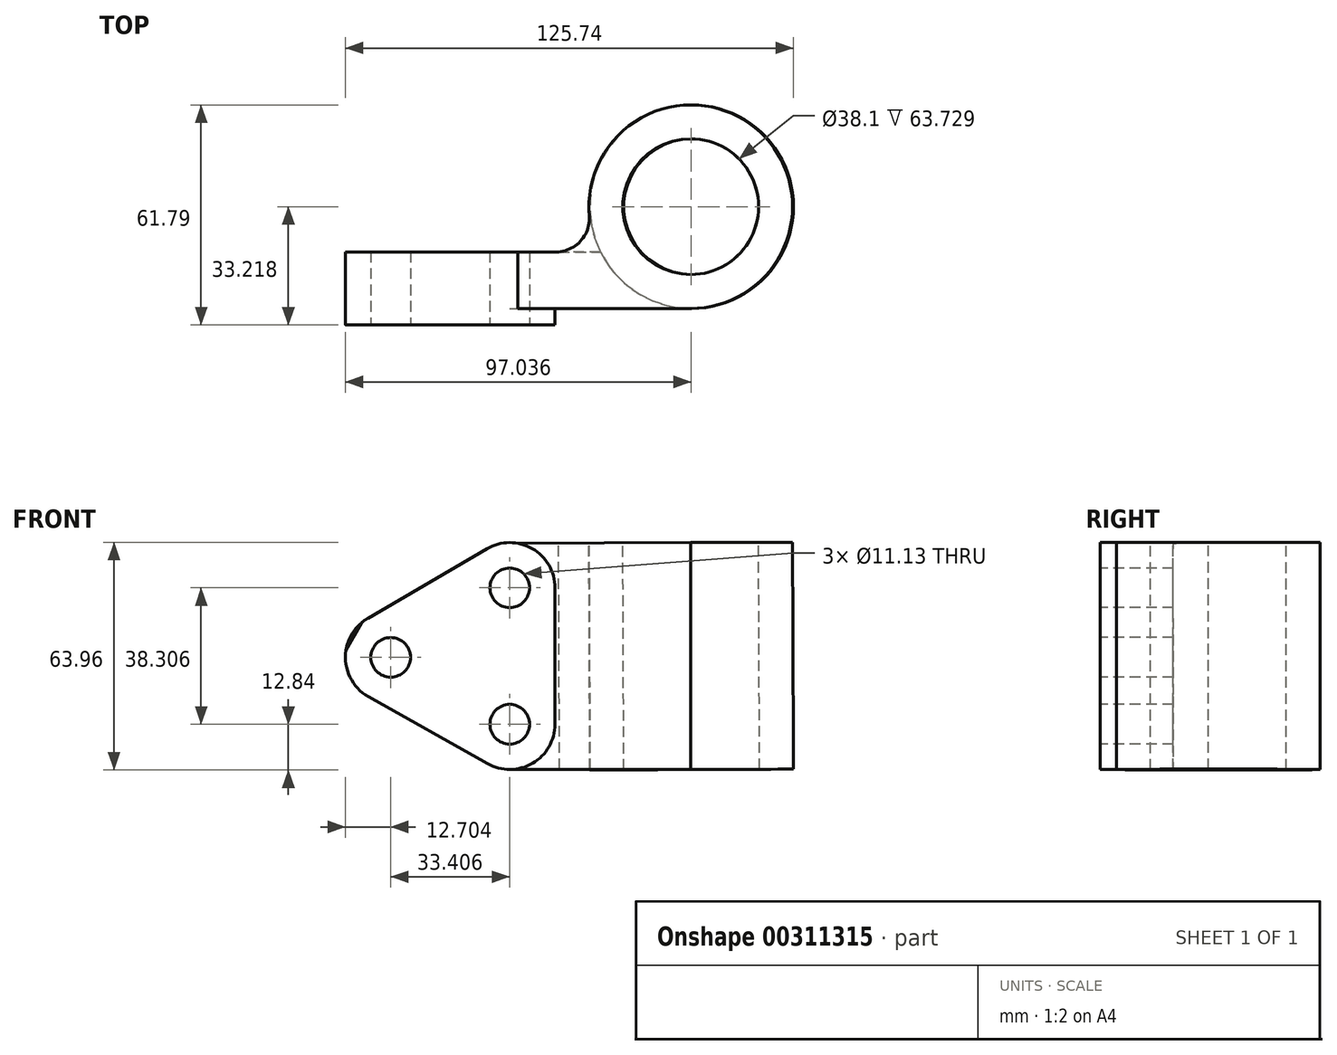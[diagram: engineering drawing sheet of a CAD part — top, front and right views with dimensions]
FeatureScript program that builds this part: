
annotation { "Feature Type Name" : "Feature", "Feature Type Description" : "" }
export const myFeature = defineFeature(function(context is Context, id is Id, definition is map)
    precondition{}
    {
        {
            var Q0;
            Q0=qCreatedBy(makeId("Front.planeOp"),FACE);
            var sketch = newSketch(context, id + "F0", { "sketchPlane" : qUnion([Q0])});
            skLineSegment(sketch, "E0", {"start": v(0, 0) * mm, "end": v(0, 63.5) * mm});
            skLineSegment(sketch, "E1", {"start": v(0, 0) * mm, "end": v(50.8, 0) * mm});
            skLineSegment(sketch, "E2", {"start": v(50.8, 0) * mm, "end": v(50.8, 63.7) * mm});
            skLineSegment(sketch, "E3", {"start": v(50.8, 63.7) * mm, "end": v(0, 63.5) * mm});
            skSolve(sketch);
        }
        {
            var Q0;
            Q0 = qSketchRegion(id + "F0", true);
            extrude(context, id + "F1", {"entities" : qUnion([Q0]), "endBound" : BoundingType.SYMMETRIC, "depth" : 15.88 * mm});
        }
        {
            var Q0;
            Q0=makeQuery(id+"F1.opExtrude","CAP_FACE",FACE,{"disambiguationData":[OSD([sQuery(id+"F0.wireOp",EDGE,"E0"),sQuery(id+"F0.wireOp",EDGE,"E1"),sQuery(id+"F0.wireOp",EDGE,"E2"),sQuery(id+"F0.wireOp",EDGE,"E3")])],"isStart":false});
            var sketch = newSketch(context, id + "F2", { "sketchPlane" : qUnion([Q0])});
            skCircle(sketch, "E4", {"center": v(-33.4, 31.49) * mm, "radius": 12.7 * mm});
            skCircle(sketch, "E5", {"center": v(0, 12.7) * mm, "radius": 12.7 * mm});
            skCircle(sketch, "E6", {"center": v(0, 51) * mm, "radius": 12.7 * mm});
            skLineSegment(sketch, "E7", {"start": v(-39.63, 20.42) * mm, "end": v(-6.23, 1.63) * mm});
            skLineSegment(sketch, "E8", {"start": v(-39.81, 42.46) * mm, "end": v(-6.4, 61.97) * mm});
            skLineSegment(sketch, "E9", {"start": v(12.7, 51) * mm, "end": v(12.7, 12.7) * mm});
            skSolve(sketch);
        }
        {
            var Q0;
            Q0 = qSketchRegion(id + "F2", true);
            extrude(context, id + "F3", {"entities" : qUnion([Q0]), "operationType" : NewBodyOperationType.ADD, "endBound" : BoundingType.SYMMETRIC, "oppositeDirection" : true, "depth" : 31.75 * mm});
        }
        {
            var Q0;
            Q0=makeQuery(id+"F3.opExtrude","SWEPT_FACE",FACE,{"disambiguationData":[OSD([sQuery(id+"F2.wireOp",EDGE,"E7")])]});
            var sketch = newSketch(context, id + "F4", { "sketchPlane" : qUnion([Q0])});
            skLineSegment(sketch, "E10", {"start": v(15.5, 7.79) * mm, "end": v(15.5, 12.56) * mm, "construction": true});
            skLineSegment(sketch, "E11", {"start": v(15.5, 12.56) * mm, "end": v(-56.45, 12.56) * mm});
            skLineSegment(sketch, "E12", {"start": v(-56.45, 12.56) * mm, "end": v(-56.45, 26.24) * mm});
            skLineSegment(sketch, "E13", {"start": v(-56.45, 26.24) * mm, "end": v(15.5, 26.24) * mm});
            skLineSegment(sketch, "E14", {"start": v(15.5, 26.24) * mm, "end": v(15.5, 12.56) * mm});
            skSolve(sketch);
        }
        {
            var Q0;
            Q0 = qSketchRegion(id + "F4", true);
            extrude(context, id + "F5", {"entities" : qUnion([Q0]), "operationType" : NewBodyOperationType.REMOVE, "oppositeDirection" : true, "depth" : 87.88 * mm});
        }
        {
            var Q0;
            Q0=qCreatedBy(makeId("Top.planeOp"),FACE);
            var sketch = newSketch(context, id + "F6", { "sketchPlane" : qUnion([Q0])});
            skLineSegment(sketch, "E15", {"start": v(-41.44, -12.58) * mm, "end": v(-46.1, -12.58) * mm});
            skLineSegment(sketch, "E16", {"start": v(-46.1, -12.58) * mm, "end": v(-46.1, -26.86) * mm});
            skLineSegment(sketch, "E17", {"start": v(-46.1, -26.86) * mm, "end": v(-39.63, -26.86) * mm});
            skLineSegment(sketch, "E18", {"start": v(-39.63, -26.86) * mm, "end": v(-39.63, -12.58) * mm});
            skLineSegment(sketch, "E19", {"start": v(-39.63, -12.58) * mm, "end": v(-46.1, -12.58) * mm});
            skSolve(sketch);
        }
        {
            var Q0;
            Q0 = qSketchRegion(id + "F6", true);
            extrude(context, id + "F7", {"entities" : qUnion([Q0]), "operationType" : NewBodyOperationType.REMOVE, "depth" : 84.58 * mm});
        }
        {
            var Q0;
            Q0=makeQuery(id+"F5.boolean.opBoolean","COPY",FACE,{"derivedFrom":makeQuery(id+"F5.opExtrude","SWEPT_FACE",FACE,{"disambiguationData":[OSD([sQuery(id+"F4.wireOp",EDGE,"E11")])]})});
            var sketch = newSketch(context, id + "F8", { "sketchPlane" : qUnion([Q0])});
            skCircle(sketch, "E20", {"center": v(0, 51) * mm, "radius": 5.56 * mm});
            skCircle(sketch, "E21", {"center": v(0, 12.7) * mm, "radius": 5.56 * mm});
            skCircle(sketch, "E22", {"center": v(-33.4, 31.49) * mm, "radius": 5.56 * mm});
            skSolve(sketch);
        }
        {
            var Q0;
            Q0 = qSketchRegion(id + "F8", true);
            extrude(context, id + "F9", {"entities" : qUnion([Q0]), "operationType" : NewBodyOperationType.REMOVE, "oppositeDirection" : true, "depth" : 25.4 * mm});
        }
        {
            var Q0;
            Q0=makeQuery(id+"F1.opExtrude","SWEPT_FACE",FACE,{"disambiguationData":[OSD([sQuery(id+"F0.wireOp",EDGE,"E3")])]});
            var sketch = newSketch(context, id + "F10", { "sketchPlane" : qUnion([Q0])});
            skCircle(sketch, "E23", {"center": v(51.06, 20.64) * mm, "radius": 28.58 * mm});
            skSolve(sketch);
        }
        {
            var Q0;
            Q0 = qSketchRegion(id + "F10", true);
            extrude(context, id + "F11", {"entities" : qUnion([Q0]), "operationType" : NewBodyOperationType.ADD, "oppositeDirection" : true, "depth" : 63.73 * mm});
        }
        {
            var Q0;
            Q0=makeQuery(id+"F11.boolean.opBoolean","MERGE",FACE,{"derivedFrom":[makeQuery(id+"F1.opExtrude","SWEPT_FACE",FACE,{"disambiguationData":[OSD([sQuery(id+"F0.wireOp",EDGE,"E3")])]}),makeQuery(id+"F11.opExtrude","CAP_FACE",FACE,{"disambiguationData":[OSD([sQuery(id+"F10.wireOp",EDGE,"E23")])],"isStart":true})]});
            var sketch = newSketch(context, id + "F12", { "sketchPlane" : qUnion([Q0])});
            skCircle(sketch, "E24", {"center": v(51.06, 20.64) * mm, "radius": 19.05 * mm});
            skSolve(sketch);
        }
        {
            var Q0;
            Q0 = qSketchRegion(id + "F12", true);
            extrude(context, id + "F13", {"entities" : qUnion([Q0]), "operationType" : NewBodyOperationType.REMOVE, "oppositeDirection" : true, "depth" : 95.76 * mm});
        }
        {
            var Q0;
            Q0=makeQuery(id+"F11.boolean.opBoolean","MERGE",FACE,{"derivedFrom":[makeQuery(id+"F1.opExtrude","SWEPT_FACE",FACE,{"disambiguationData":[OSD([sQuery(id+"F0.wireOp",EDGE,"E3")])]}),makeQuery(id+"F11.opExtrude","CAP_FACE",FACE,{"disambiguationData":[OSD([sQuery(id+"F10.wireOp",EDGE,"E23")])],"isStart":true})]});
            var sketch = newSketch(context, id + "F14", { "sketchPlane" : qUnion([Q0])});
            skArc(sketch, "E25", {"start": v(12.24, 7.94) * mm, "mid": v(19.96, 10.81) * mm, "end": v(22.55, 18.63) * mm});
            skLineSegment(sketch, "E26", {"start": v(22.55, 18.63) * mm, "end": v(25.46, 7.94) * mm});
            skLineSegment(sketch, "E27", {"start": v(25.46, 7.94) * mm, "end": v(12.24, 7.94) * mm});
            skSolve(sketch);
        }
        {
            var Q0;
            Q0 = qSketchRegion(id + "F14", true);
            extrude(context, id + "F15", {"entities" : qUnion([Q0]), "operationType" : NewBodyOperationType.ADD, "oppositeDirection" : true, "depth" : 63.5 * mm});
        }
    });
